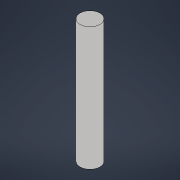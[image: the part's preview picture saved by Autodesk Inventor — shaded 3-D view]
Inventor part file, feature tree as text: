
AUTODESK INVENTOR PART (.ipt)
format: ipt  version: 2021 (Build 250183000, 183)  size: 87,552 bytes
history: native  units: mm
features: other x2, extrude x1, sketch x1
ambient origin geometry x8: Origin, YZ Plane, XZ Plane, XY Plane, X Axis, Y Axis, Z Axis, Center Point
bodies: Body1 (feature_tree)
feature tree (4):
  other  "Eixo Médio - Engrenagem"
  other  "Sólido1"
  extrude  "Extrusão1"  Depth=5.6mm TaperAngle=0.0deg
  sketch  "Esboço1"  dims[d0=0.9mm d1=5.6mm d2=0.0mm]
